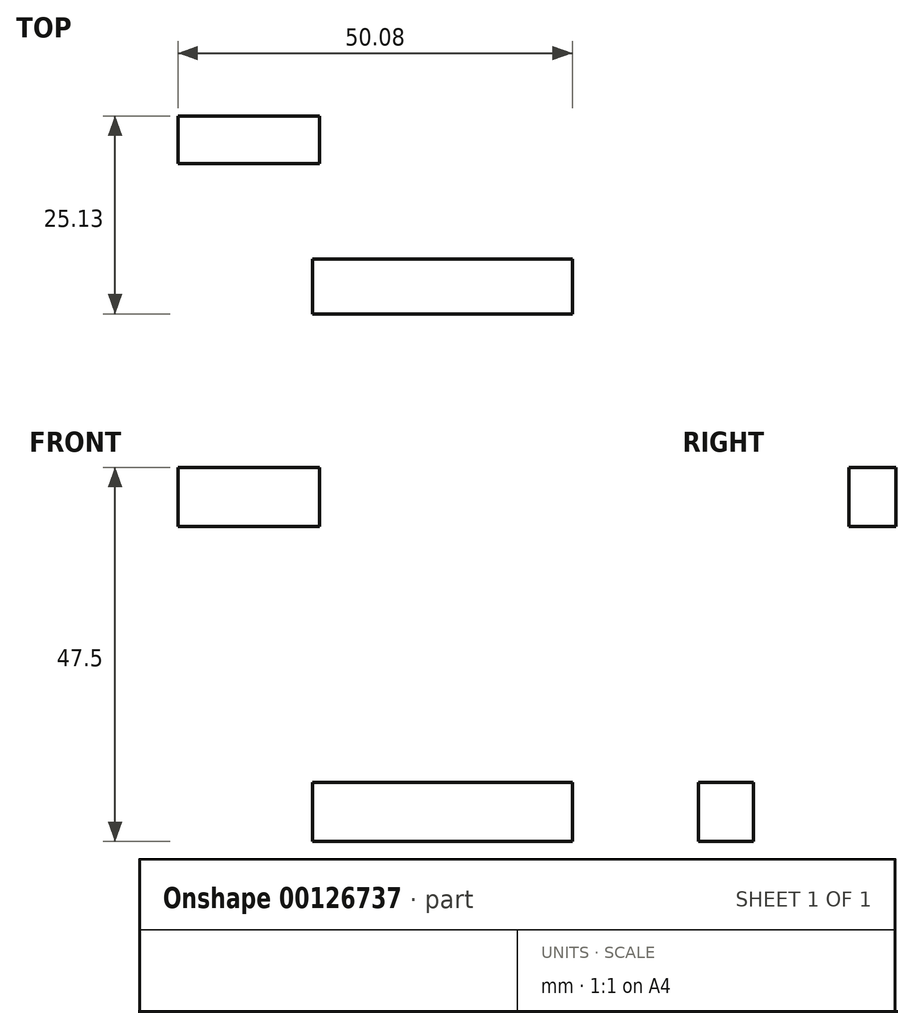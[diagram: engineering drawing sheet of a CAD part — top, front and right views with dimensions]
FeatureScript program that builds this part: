
annotation { "Feature Type Name" : "Feature", "Feature Type Description" : "" }
export const myFeature = defineFeature(function(context is Context, id is Id, definition is map)
    precondition{}
    {
        {
            var Q0;
            Q0=qCreatedBy(makeId("Top.planeOp"),FACE);
            var sketch = newSketch(context, id + "F0", { "sketchPlane" : qUnion([Q0])});
            skLineSegment(sketch, "E0.bottom", {"start": v(-20.93, 12.15) * mm, "end": v(12.07, 12.15) * mm});
            skLineSegment(sketch, "E0.top", {"start": v(-20.93, 5.15) * mm, "end": v(12.07, 5.15) * mm});
            skLineSegment(sketch, "E0.left", {"start": v(-20.93, 12.15) * mm, "end": v(-20.93, 5.15) * mm});
            skLineSegment(sketch, "E0.right", {"start": v(12.07, 12.15) * mm, "end": v(12.07, 5.15) * mm});
            skSolve(sketch);
        }
        {
            var Q0;
            Q0=makeQuery(id+"F0.imprint","IMPRINT",FACE,{"disambiguationData":[TD([[makeQuery(id+"F0.imprint","IMPRINT",EDGE,{"derivedFrom":sQuery(id+"F0.wireOp",EDGE,"E0.bottom")}),-1.0]])]});
            extrude(context, id + "F1", {"entities" : qUnion([Q0]), "depth" : 7.5 * mm});
        }
        {
            var Q0;
            Q0=qCreatedBy(makeId("Top.planeOp"),FACE);
            cPlane(context, id + "F2", {"entities" : qUnion([Q0]), "cplaneType" : CPlaneType.OFFSET, "offset" : 40 * mm, "width" : 150 * mm, "height" : 150 * mm});
        }
        {
            var Q0;
            Q0=qCreatedBy(id+"F2.planeOp",FACE);
            var sketch = newSketch(context, id + "F3", { "sketchPlane" : qUnion([Q0])});
            skLineSegment(sketch, "E1.bottom", {"start": v(-38.01, 30.28) * mm, "end": v(-20.01, 30.28) * mm});
            skLineSegment(sketch, "E1.top", {"start": v(-38.01, 24.28) * mm, "end": v(-20.01, 24.28) * mm});
            skLineSegment(sketch, "E1.left", {"start": v(-38.01, 30.28) * mm, "end": v(-38.01, 24.28) * mm});
            skLineSegment(sketch, "E1.right", {"start": v(-20.01, 30.28) * mm, "end": v(-20.01, 24.28) * mm});
            skSolve(sketch);
        }
        {
            var Q0;
            Q0=makeQuery(id+"F3.imprint","IMPRINT",FACE,{"disambiguationData":[TD([[makeQuery(id+"F3.imprint","IMPRINT",EDGE,{"derivedFrom":sQuery(id+"F3.wireOp",EDGE,"E1.bottom")}),-1.0]])]});
            extrude(context, id + "F4", {"entities" : qUnion([Q0]), "depth" : 7.5 * mm});
        }
    });
